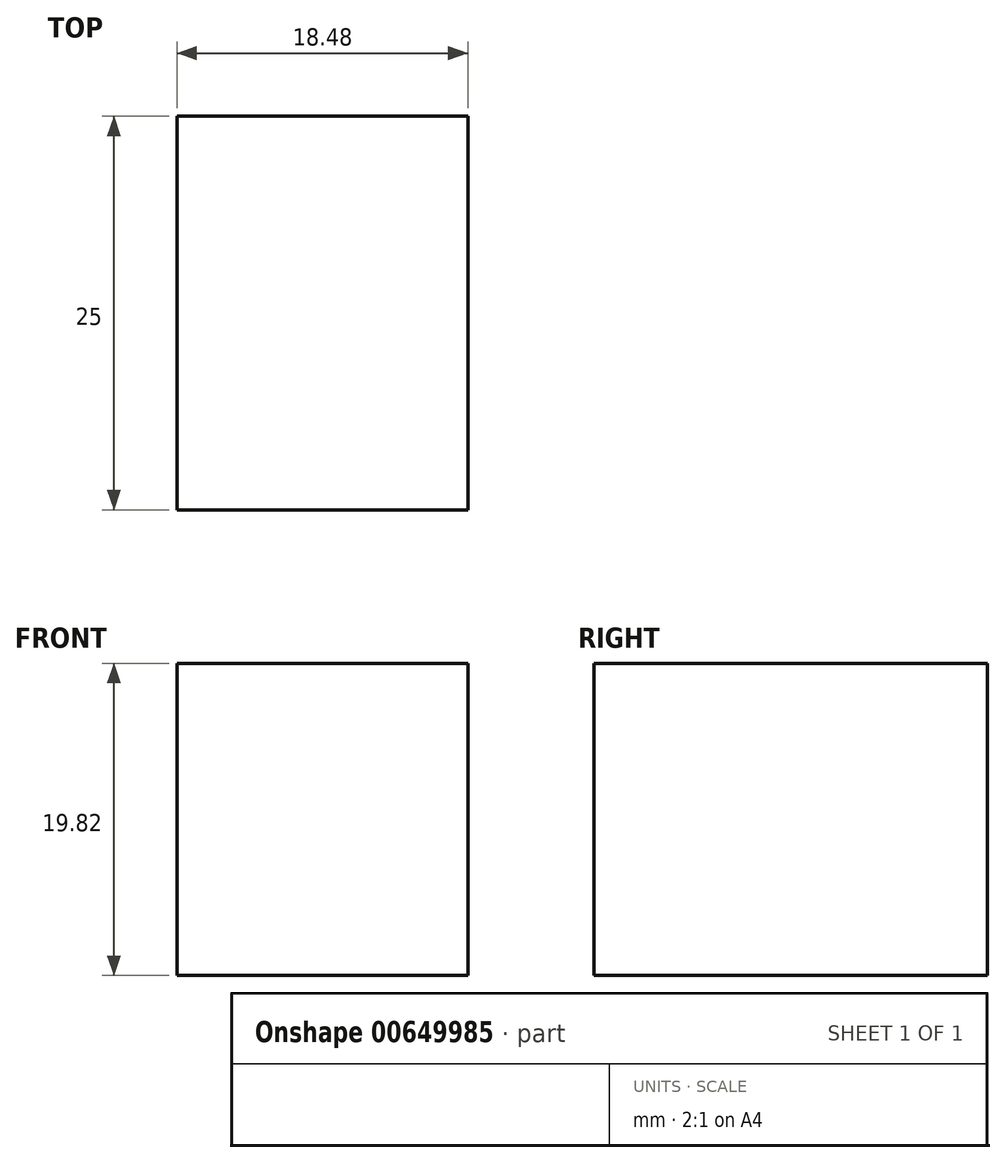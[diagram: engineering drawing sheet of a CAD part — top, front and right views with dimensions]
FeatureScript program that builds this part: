
annotation { "Feature Type Name" : "Feature", "Feature Type Description" : "" }
export const myFeature = defineFeature(function(context is Context, id is Id, definition is map)
    precondition{}
    {
        {
            var Q0;
            Q0=qCreatedBy(makeId("Front.planeOp"),FACE);
            var sketch = newSketch(context, id + "F0", { "sketchPlane" : qUnion([Q0])});
            skLineSegment(sketch, "E0.bottom", {"start": v(-55.28, 38.81) * mm, "end": v(-36.8, 38.81) * mm});
            skLineSegment(sketch, "E0.top", {"start": v(-55.28, 18.99) * mm, "end": v(-36.8, 18.99) * mm});
            skLineSegment(sketch, "E0.left", {"start": v(-55.28, 38.81) * mm, "end": v(-55.28, 18.99) * mm});
            skLineSegment(sketch, "E0.right", {"start": v(-36.8, 38.81) * mm, "end": v(-36.8, 18.99) * mm});
            skSolve(sketch);
        }
        {
            var Q0;
            Q0 = qSketchRegion(id + "F0", true);
            extrude(context, id + "F1", {"entities" : qUnion([Q0]), "depth" : 25 * mm, "offsetDistance" : 25 * mm});
        }
    });
